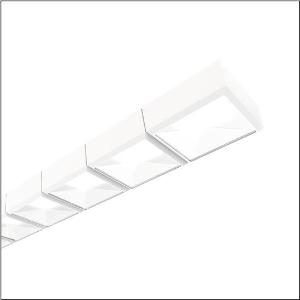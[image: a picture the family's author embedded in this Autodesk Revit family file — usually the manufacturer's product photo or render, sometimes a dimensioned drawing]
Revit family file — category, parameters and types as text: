
# Revit family: scriptus_r__11_5mz312d04wa_0fc2
name_source: partatom
category: Lighting Fixtures
units: mm (PartAtom-declared; Revit-internal decimal feet)

## family parameters
Cut with Voids When Loaded = No
Host = Face
Light Source = No
Part Type = Normal
Room Calculation Point = No
Round Connector Dimension = Use Diameter
Shared = No

## types (1)
- Scriptus® 11 (1 x LED 4000K / CRI = 80 (unbekannt), 1610 lm / 2410 lm, 4000K)
    Apparent Load = 62 VA
    CIE Flux Codes = - - - 0 100 / 82 95 99 100 100
    Color Rendering = 80
    Color Temperature = 4000K
    Default Elevation = 1800 mm
    Description = Scriptus® 11, office luminaire, primary optical cover: lenses, CAT 2 (L<= 3000cd/m²), light emission: direct/indirect distribution, primary light characteristic: symmetric, installation type: suspended mounting, LED, rated luminous flux: 8.020lm, luminous efficacy: 130lm/W, light colour: 840, colour temperature: 4000K, control gear: ECG DALI, with terminal, 5-pole, mains connection: 230V, AC, 50Hz, rated input power: 62W, LED, control gear: ECG DALI, housing, luminaire housing, of aluminium, traffic white (RAL 9016), length: 1.658mm, width: 114mm, height: 57mm, protection rating (complete): IP20, insulation class (complete): insulation class I (protective earthing), certification: CE, ENEC, VDE, protection symbol: F, permissible operating ambient temperature: 0..+35°C, standard: EN 50419, packaging unit: 1 piece
    Height = 57 mm
    Lamp = 1 x LED 4000K / CRI >= 80 (unbekannt)
    Lamp Light Flux = 1610 lm / 2410 lm
    Lamp count = 1
    Length = 1658 mm
    Luminous efficacy = 131 lm/W
    Manufacturer = Siteco
    ModVariant = No
    Model = 5MZ312D04WA
    Mounting Place = Ceiling
    Mounting Type = Pendant
    Number of Poles = 1
    OnlyDefault = Yes
    Power Factor = 1
    Product Name = Scriptus® 11
    Product group = office luminaire | ceiling pendant
    ProductGroupID = 902
    Protection Class = Protection class I
    Protection Degree = IP 20
    RLX_Detail_Level = 1
    RLX_Emergency_Light_Flux = 0 lm
    RLX_Emergency_Type = 0
    RLX_Emergency_Type_DB = No
    RlxData = <blob elided: 31157 chars, md5=e1607eca>
    Socket = socket
    Standby Power = 0 W
    System Light Flux = 8040 lm
    System Power = 62 W
    Type Comments = Product without accessories
    Type Image = l_1004839.jpg
    URL = http://relux.com
    VarID = ---
    Voltage = 0 V
    Weight = 0.00 kg
    Width = 114 mm

## geometry (parser evidence)
native form markers: Blend x4, Sweep x18
no freeform markers — native parametric forms only
